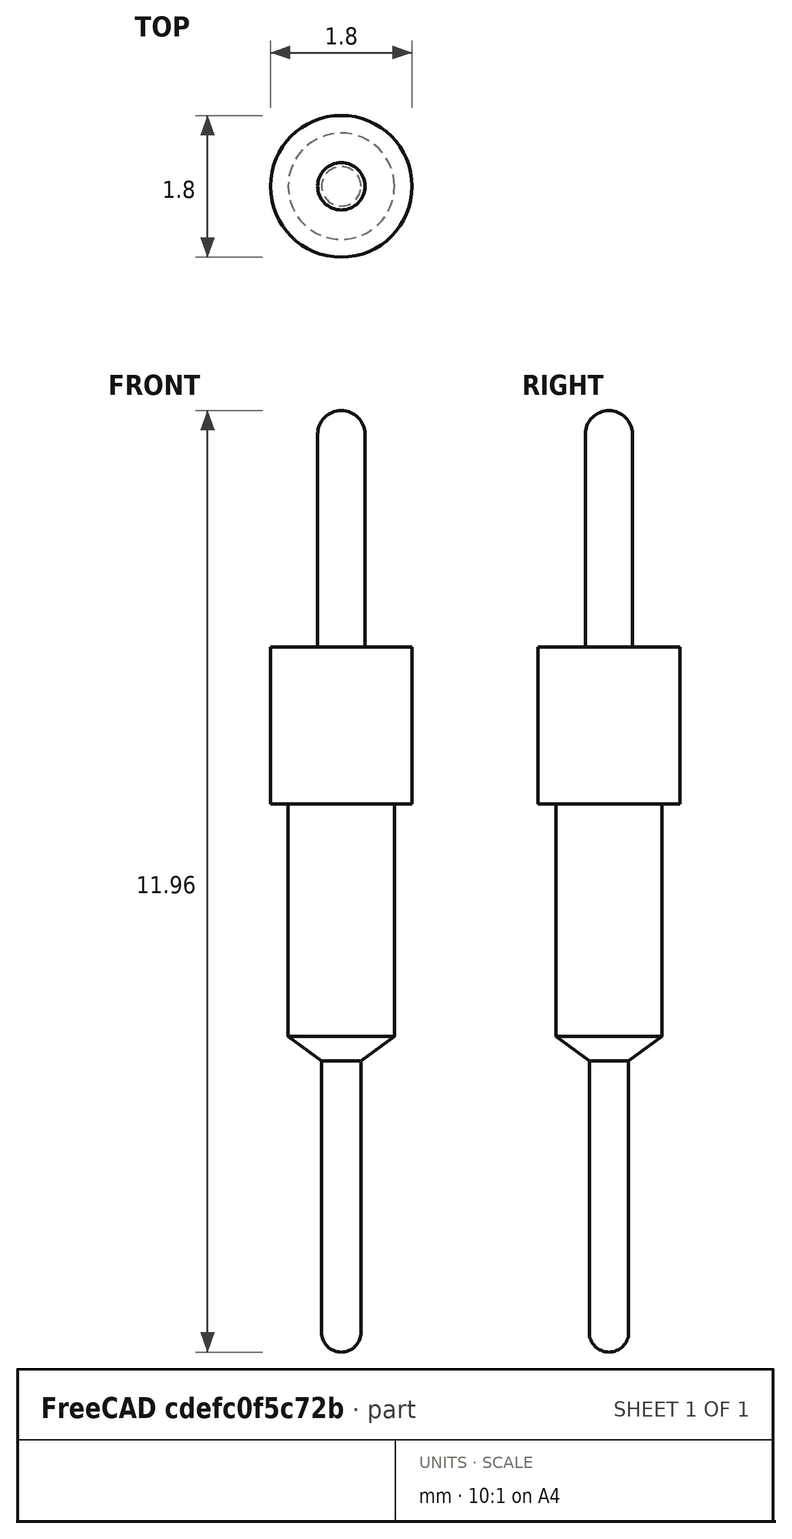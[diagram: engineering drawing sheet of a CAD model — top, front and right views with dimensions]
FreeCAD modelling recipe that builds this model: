
FCSTD DOCUMENT  (FreeCAD 0.21R33771 (Git))
Label: Connfly_DS-1006-11
License: All rights reserved
LicenseURL: https://en.wikipedia.org/wiki/All_rights_reserved
objects: Sketcher::SketchObject×1, PartDesign::Revolution×1, PartDesign::Body×1
note: 4 computed .brp shape members not serialized (recipe doc carries the construction recipe); baked Part::Feature solids carry a one-line shape summary decoded from their .brp

FEATURE [Sketcher::SketchObject] Sketch
  FullyConstrained = true
  MapMode = 5
  Placement = pos=(0,0,0) rot=(1,0,0;1.5708rad)
  Support = -> [XZ_Plane]
  sketch-geometry (11):
    g0: LineSegment StartX=-1.38e-14 StartY=8.26 StartZ=0 EndX=-1.38e-14 EndY=-3.7 EndZ=0
    g1: LineSegment StartX=-0.3 StartY=7.96 StartZ=0 EndX=-0.3 EndY=5.26 EndZ=0
    g2: LineSegment StartX=-0.3 StartY=5.26 StartZ=0 EndX=-0.9 EndY=5.26 EndZ=0
    g3: LineSegment StartX=-0.9 StartY=5.26 StartZ=0 EndX=-0.9 EndY=3.26 EndZ=0
    g4: LineSegment StartX=-0.9 StartY=3.26 StartZ=0 EndX=-0.675 EndY=3.26 EndZ=0
    g5: LineSegment StartX=-0.675 StartY=3.26 StartZ=0 EndX=-0.675 EndY=0.31 EndZ=0
    g6: LineSegment StartX=-0.675 StartY=0.31 StartZ=0 EndX=-0.25 EndY=0 EndZ=0
    g7: LineSegment StartX=-0.25 StartY=0 StartZ=0 EndX=-0.25 EndY=-3.45 EndZ=0
    g8: ArcOfCircle CenterX=-1.08e-14 CenterY=7.96 CenterZ=0 NormalX=0 NormalY=0 NormalZ=1 AngleXU=0 Radius=0.3 StartAngle=1.5708 EndAngle=3.14159
    g9: ArcOfCircle CenterX=-1.38e-14 CenterY=-3.45 CenterZ=0 NormalX=0 NormalY=0 NormalZ=1 AngleXU=0 Radius=0.25 StartAngle=3.14159 EndAngle=4.71239
    g10: GeomPoint X=0 Y=0 Z=0
  constraints (33):
    c: Vertical(g0)
    c: Vertical(g1)
    c: Coincident(g1,g2)
    c: Horizontal(g2)
    c: Coincident(g2,g3)
    c: Vertical(g3)
    c: Coincident(g3,g4)
    c: Coincident(g4,g5)
    c: Vertical(g5)
    c: Coincident(g5,g6)
    c: Coincident(g6,g7)
    c: Vertical(g7)
    c: Coincident(g8,g1)
    c: Coincident(g9,g7)
    c: Horizontal(g4)
    c: Vertical(g9,g0)
    c: Angle(g8) = 1.5708
    c: Angle(g9) = 1.5708
    c: Horizontal(g8,g1)
    c: DistanceX(g7,g9) = 0.25
    c: DistanceY(g2,g0) = 3
    c: DistanceY(g3,g0) = 5
    c: DistanceY(g5,g0) = 7.95
    c: DistanceY(g6,g0) = 8.26
    c: DistanceY(g0,g0) = 11.96
    c: DistanceX(g1,g0) = 0.3
    c: DistanceX(g2,g0) = 0.9
    c: DistanceX(g4,g0) = 0.675
    c: Coincident(g0,g9)
    c: Coincident(g8,g0)
    c: PointOnObject(g10,g0)
    c: Horizontal(g10,g6)
    c: Coincident(g10,g-1)
FEATURE [PartDesign::Revolution] Revolution
  Angle = 360
  Axis = (0,2e-16,1)
  Base = (0,0,0)
  Placement = pos=(0,0,0) rot=(1,0,0;1.5708rad)
  Profile = -> Sketch
  ReferenceAxis = -> Sketch [V_Axis]
FEATURE [PartDesign::Body] Body
  Group = -> [Sketch,Revolution]
  Origin = -> Origin
  Tip = -> Revolution
